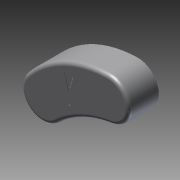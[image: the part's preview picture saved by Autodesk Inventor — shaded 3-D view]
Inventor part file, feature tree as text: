
AUTODESK INVENTOR PART (.ipt)
format: ipt  version: 2012 SP1 (Build 160190100, 190)  size: 120,320 bytes
history: native  units: in
note: dims shown in document units (in); Inventor stores cm internally (conversion verified against a paired STEP export)
features: extrude x2, sketch x2, fillet x1
ambient origin geometry x8: Origin, YZ Plane, XZ Plane, XY Plane, X Axis, Y Axis, Z Axis, Center Point
feature tree (5):
  extrude  "Extrusion2"  Depth=0.025in
  fillet  "Fillet5"  Radius=0.0025in
  extrude  "Extrusion3"  [1 undecoded]
  sketch  "Sketch2"  dims[d7=0.2in d8=0.0in d9=0.025in d10=0.0025in d11=0.0in]
  sketch  "Sketch3"
note: 1 required parameter value undecoded (feature->parameter linkage not recoverable at this tier; creation-order binding heuristic only, values carry confidence <= 0.55)
